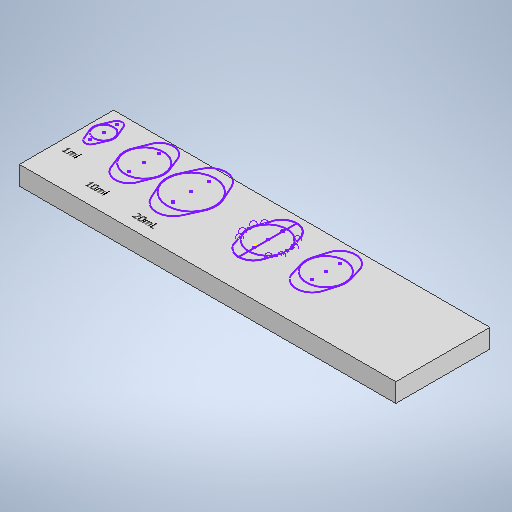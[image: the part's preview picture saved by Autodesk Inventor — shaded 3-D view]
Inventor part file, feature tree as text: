
AUTODESK INVENTOR PART (.ipt)
format: ipt  version: 2025 (Build 290162000, 162)  size: 262,656 bytes
history: native  units: mm
features: sketch x2, extrude x1
ambient origin geometry x8: Origin, YZ Plane, XZ Plane, XY Plane, X Axis, Y Axis, Z Axis, Center Point
bodies: Volumenkörper1 (feature_tree)
feature tree (3):
  extrude  "Extrusion1"  Depth=50.0mm
  sketch  "Skizze2"  dims[d2=10.0mm d3=0.0mm]
  sketch  "Skizze1"  dims[d0=200.0mm d1=50.0mm]
